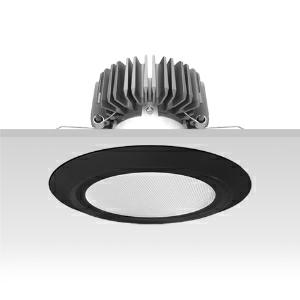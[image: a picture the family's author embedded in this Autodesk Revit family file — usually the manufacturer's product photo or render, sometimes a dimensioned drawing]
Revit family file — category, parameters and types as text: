
# Revit family: 3f_filippi_-_3f_reno_bianco_ampio_3f_filippi_-_30621_a01038_-_3f_reno_200_wh_2000-840_wide___vs_bk_8d46
name_source: partatom
category: Lighting Fixtures
units: mm (PartAtom-declared; Revit-internal decimal feet)

## family parameters
Cut with Voids When Loaded = No
Host = Face
Light Source = No
Part Type = Normal
Room Calculation Point = No
Round Connector Dimension = Use Diameter
Shared = No

## types (1)
- 3F Filippi - 3F Reno Bianco Ampio (1 x LED, 1723 lm, 20 W, 4000 K)
    Apparent Load = 20 VA
    Approval mark = CE
    CIE Flux Codes = 75 94 99 100 100
    Color Rendering = 80
    Color Temperature = 4000 K
    Control Gear = Electronic ballast
    Default Elevation = 1800 mm
    Description = ILLUMINOTECHNICAL
Luminous efficiency 100% (DLOR 100%, ULOR 0%).
Initial luminous flux of the luminaire 1723 lm.
Direct symmetric wide distribution.
Installation Interdistance Transv.D = 1.16 x hu - Long.D = 1.14 x hu.
Average luminance <3000 cd/m² for radial angles >65°.
Tabular UGR (CIE 117 - 4H-8H; S=0.25H; 70/50/20): RUG 20.4 - 20.3.
Beam angle: 74° - 74°.
Luminous efficacy 86 lm/W.
Lifetime (L90/B10): 30000 h. (tq+25°C)
Lifetime (L85/B10): 50000 h. (tq+25°C)
Lifetime (L70/B10): 80000 h. (tq+25°C)
Sudden decreased luminous flux after 50000 hours: 0% (C0).
Photobiological safety in compliance with IEC/TR 62778: RG0 risk exempt, (IEC 62471).
In compliance with IEC/EN 62722-2-1 - IEC/EN 62717 standards.

SOURCE
Compact LED module 2000/840.
Energy efficiency class (UE 2019/2020 - UE 2019/2015): D.
CIE 13.3 Colour rendering index: CRI >80 (R9 <50%).
IES TM-30 Fidelity Index: Rf = 84 Rg = 95.
CCT nominal colour temperature 4000 K.
Colour initial tolerance (MacAdam): SDCM 3.
Zhaga Book 3 compliant.

MECHANICAL
Passive heat dissipator in die-casting aluminium, oversized, for optimum thermal management of the LED module.
Parabolic element with graduated/concentric rings in white polycarbonate.
Transparent external lens with glossy and satin differentiated surfaces, with a cooling and anti-insect system in methacrylate (PMMA).
Fastening spring clips in stainless steel.
Dimensions: diameter 226 mm, height 146 mm. Weight 1.13 kg.
IP44 protection degree for exposed part, IP20 for recessed part.
Mechanical strength to impacts IK06 (1 joule).
Glow-wire test resistance 650°C.

ELECTRICAL
Wiring on a separate unit.
Halogen Free electronic wiring 230V-50/60Hz, power factor 0.95, THD <25%, constant output current, SELV, class II, 1 driver.
Power of the luminaire 20 W.
ENEC - CE.
SAFE FLICKER: PstLM=<1 and SVM=<0.4 (IEC TR 61547-1 and IEC TR 63158), to ensure a more comfortable and safe light.
Luminaire compliant with EN 60598-2-22 for power supply from a centralised emergency system CPSS (Central Power Supply System), not incorporated in the luminaire - high risk areas excluded. The default power and flux are 100% in AC and 100% in DC.
Ambient temperature from 0°C to +25°C.
Temperature class T6 max 85°C.
Relative humidity UR: <85%.

INSTALLATION
Pull-up recessed fitting.
False ceiling carving: 200 mm.
All accessories dedicated to this product are available on the Catalog and on our website www.3F-Filippi.com.

ACCESSORIES
A01038 - Anti-glare microprismatic VS moulded glass, tempered, not flammable, locked and in line with the trim, in black polycarbonate.

APPLICATIONS
Environments: architectural, commercial, exhibition areas, transit areas, corridors, shops, display windows, service areas.
In false ceilings with narrow voids.

WARNING
Luminaire designed for disposal/recycling at end-of-life.
Replaceable (LED only) light source by a professional. Replaceable control gear by a professional.
    Height = 0 mm  [stored 0 ft]
    Lamp = 1 x LED
    Lamp Light Flux = 1723 lm
    Lamp Power = 20 W
    Lamp count = 1
    Length = 226 mm
    Lifetime = 50000 h
    Luminous efficacy = 86 lm/W
    Manufacturer = 3F Filippi
    ModVariant = No
    Model = 3F Filippi - 30621+A01038 - 3F Reno 200 WH 2000-840 WIDE + VS BK
    Mounting Place = Ceiling
    Mounting Type = Recessed
    Number of Poles = 1
    OnlyDefault = Yes
    Power Factor = 1
    Product Name = 3F Filippi - 3F Reno Bianco Ampio
    Product group = recessed luminaire
    ProductGroupID = 4
    Protection Class = Protection class II
    Protection Degree = IP 20
    RLX_Detail_Level = 1
    RLX_Emergency_Light_Flux = 0 lm
    RLX_Emergency_Type = 0
    RLX_Emergency_Type_DB = No
    RlxData = <blob elided: 97389 chars, md5=750b7d1d>
    Socket = socket
    Standby Power = 0 W
    System Light Flux = 1723 lm
    System Power = 20 W
    Type Comments = Product without accessories
    Type Image = 3ffilippi_3f_reno_200_bk_vs_smp.jpg
    URL = http://relux.com
    VarID = ---
    Voltage = 0 V
    Weight = 0.00 kg
    Width = 0 mm  [stored 0 ft]

note: [stored X ft] marks values corroborated as IEEE doubles in the binary element streams (Revit-internal decimal feet)

## geometry (parser evidence)
native form markers: Blend x4, Sweep x10
no freeform markers — native parametric forms only
